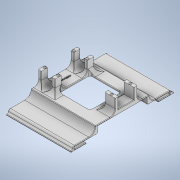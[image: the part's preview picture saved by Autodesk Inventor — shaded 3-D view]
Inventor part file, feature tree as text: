
AUTODESK INVENTOR PART (.ipt)
format: ipt  version: 2020.2 (Build 242310000, 310)  size: 826,368 bytes
history: native  units: in
note: dims shown in document units (in); Inventor stores cm internally (conversion verified against a paired STEP export)
features: sketch x14, extrude x11, fillet x8, hole x2, emboss x1
ambient origin geometry x8: Origin, YZ Plane, XZ Plane, XY Plane, X Axis, Y Axis, Z Axis, Center Point
bodies: Solid1 (feature_tree)
feature tree (36):
  extrude  "Extrusion1"  Depth=3.937in
  extrude  "Extrusion2"  Depth=0.9449in
  extrude  "Extrusion3"  TaperAngle=90.0deg  [1 undecoded]
  extrude  "Extrusion4"  Depth=1.8898in
  extrude  "Extrusion5"  Depth=0.3937in
  hole  "Hole1"  [1 undecoded]
  hole  "Hole2"  [1 undecoded]
  extrude  "Extrusion6"  Depth=0.1969in
  extrude  "Extrusion7"  Depth=0.1969in
  extrude  "Extrusion8"  Depth=0.8661in
  extrude  "Extrusion9"  Depth=0.1969in
  extrude  "Extrusion10"  Depth=0.1969in
  extrude  "Extrusion11"  Depth=0.1969in
  fillet  "Fillet1"  Radius=0.1969in
  fillet  "Fillet2"  Radius=0.1969in
  fillet  "Fillet3"  Radius=0.1969in
  fillet  "Fillet4"  Radius=0.7874in
  fillet  "Fillet5"  Radius=0.1969in
  fillet  "Fillet6"  Radius=0.1969in
  fillet  "Fillet7"  Radius=0.0984in
  fillet  "Fillet8"  Radius=0.0984in
  emboss  "Emboss1"
  sketch  "Sketch1"  dims[d0=3.937in d1=3.1102in]
  sketch  "Sketch2"  dims[d2=0.0787in d3=0.0in d4=0.9449in]
  sketch  "Sketch3"  dims[d5=0.9449in d6=90.0deg]
  sketch  "Sketch4"  dims[d7=1.8898in d8=1.8898in]
  sketch  "Sketch6"  dims[d9=0.3937in d10=0.0in d11=0.2362in]
  sketch  "Sketch7"  dims[d12=0.4724in d13=0.9449in]
  sketch  "Sketch8"  dims[d14=0.3937in d15=0.1969in d16=0.0in]
  sketch  "Sketch9"  dims[d17=0.1181in d18=0.1969in]
  sketch  "Sketch10"  dims[d19=0.1181in d20=0.1969in]
  sketch  "Sketch11"  dims[d21=0.8661in d22=0.0in d23=0.9843in]
  sketch  "Sketch12"  dims[d24=1.9685in d25=0.1969in]
  sketch  "Sketch14"  dims[d26=0.1969in d27=0.1969in]
  sketch  "Sketch16"  dims[d28=0.1969in d29=0.1969in d30=0.1969in d31=0.1969in d32=0.1969in d33=0.7874in d34=0.0in d35=0.1969in d36=0.1969in d37=0.0984in d38=0.0984in]
  sketch  "Sketch18"  dims[d39=0.1575in d40=0.2953in d41=0.4in d42=0.15in d43=90.0deg d44=0.3937in d45=0.8108in d46=0.0984in d47=0.0984in d48=0.1575in d49=0.2953in d50=0.4in d51=0.15in d52=90.0deg d53=0.3937in d54=0.8108in d55=0.0787in d56=0.1575in d57=0.0787in d58=0.1575in d59=0.3937in d60=0.0in d61=0.0787in d62=0.0in d63=0.0787in d64=1.378in d65=0.0in d66=1.378in d67=0.0in d68=0.1181in d69=0.1181in d70=0.1181in d71=0.0in d73=0.1181in d74=0.1181in d75=0.0787in d76=0.0in d77=0.1181in d78=0.3937in d79=0.1969in d80=0.315in d81=0.1181in d82=0.1181in d83=0.0315in d84=0.0315in d91=0.3937in d92=0.3937in d93=0.0394in d94=0.0in]
note: 3 required parameter values undecoded (feature->parameter linkage not recoverable at this tier; creation-order binding heuristic only, values carry confidence <= 0.55)
